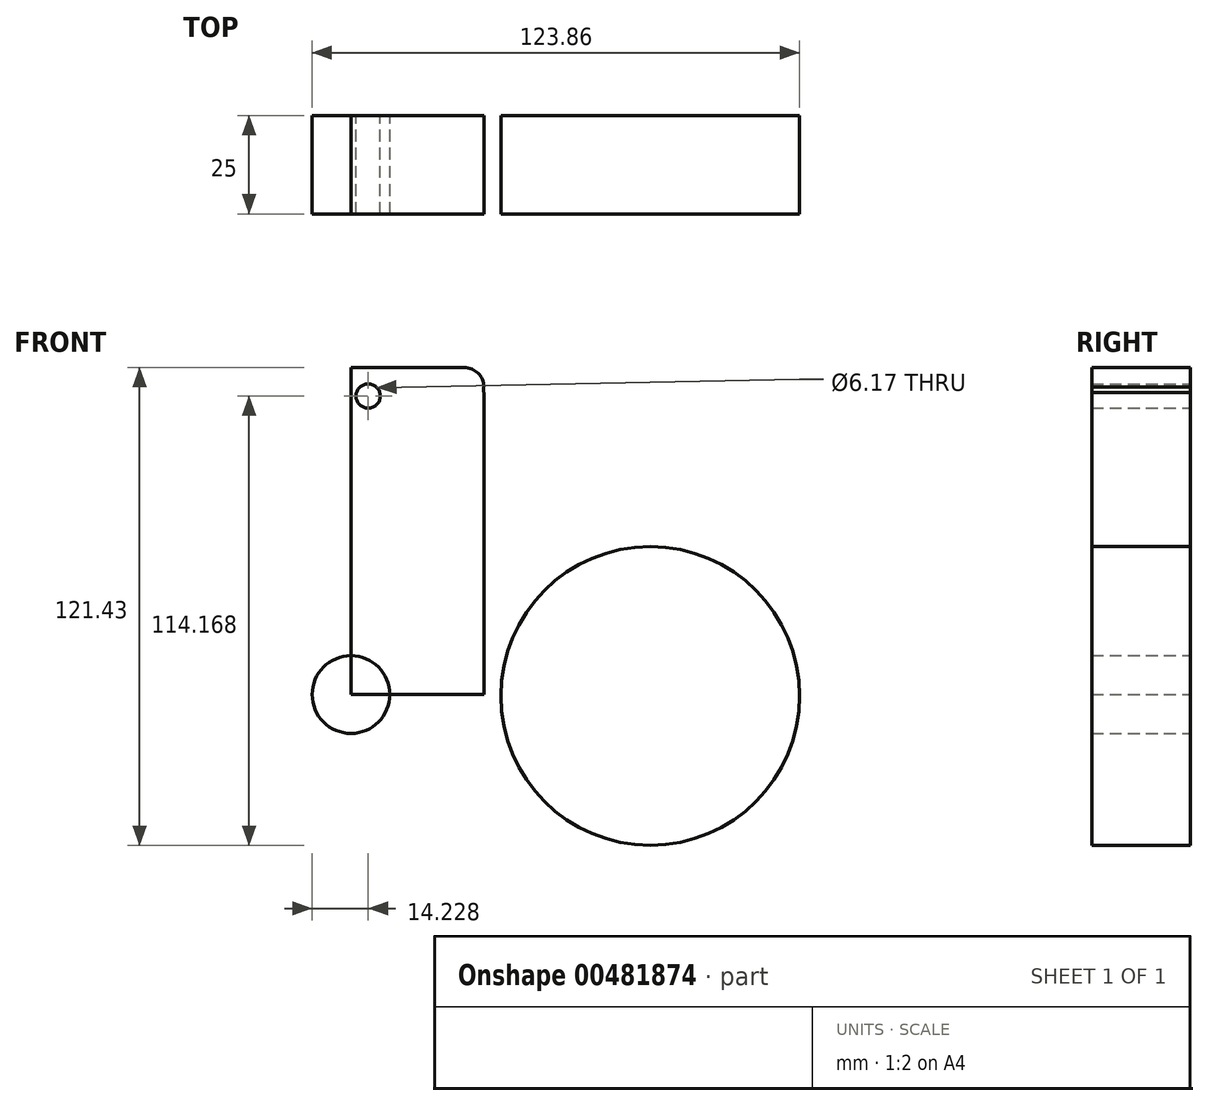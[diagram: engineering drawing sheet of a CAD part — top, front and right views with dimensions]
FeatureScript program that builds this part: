
annotation { "Feature Type Name" : "Feature", "Feature Type Description" : "" }
export const myFeature = defineFeature(function(context is Context, id is Id, definition is map)
    precondition{}
    {
        {
            var Q0;
            Q0=qCreatedBy(makeId("Front.planeOp"),FACE);
            var sketch = newSketch(context, id + "F0", { "sketchPlane" : qUnion([Q0])});
            skLineSegment(sketch, "E0.bottom", {"start": v(-17.06, -14.88) * mm, "end": v(-50.8, -14.88) * mm});
            skLineSegment(sketch, "E0.top", {"start": v(-22.06, 68.23) * mm, "end": v(-50.8, 68.23) * mm});
            skLineSegment(sketch, "E0.left", {"start": v(-17.06, -14.88) * mm, "end": v(-17.06, 63.23) * mm});
            skLineSegment(sketch, "E0.right", {"start": v(-50.8, -14.88) * mm, "end": v(-50.8, 68.23) * mm});
            skPoint(sketch, "E0.middle", {"position": v(-33.93, 26.67) * mm});
            skCircle(sketch, "E1", {"center": v(25.22, -15.24) * mm, "radius": 37.96 * mm});
            skLineSegment(sketch, "E2", {"start": v(-17.06, -14.88) * mm, "end": v(-9, -31.67) * mm});
            skCircle(sketch, "E3", {"center": v(-50.8, -14.88) * mm, "radius": 9.87 * mm});
            skPoint(sketch, "E4.visualSharp", {"position": v(-17.06, 68.23) * mm});
            skArc(sketch, "E4.filletArc", {"start": v(-17.06, 63.23) * mm, "mid": v(-18.52, 66.76) * mm, "end": v(-22.06, 68.23) * mm});
            skFitSpline(sketch, "E5", {"points": [v(-17.06, 61.88) * mm, v(-17.06, 63.23) * mm, v(15.94, 21.56) * mm], "startDerivative": vector(-2.63, 13.82) * mm, "endDerivative": vector(54.8, -73.35) * mm});
            skCircle(sketch, "E6", {"center": v(-46.45, 60.97) * mm, "radius": 3.08 * mm});
            skCircle(sketch, "E7.MirrorC", {"center": v(-46.45, 75.48) * mm, "radius": 3.08 * mm});
            skSolve(sketch);
        }
        {
            var Q0;
            {var subQ0=sQuery(id+"F0.wireOp",EDGE,"E1");var subQ1=makeQuery(id+"F0.imprint","INTERSECT",VERTEX,{"derivedFrom":[subQ0,sQuery(id+"F0.wireOp",EDGE,"E2")]});Q0=makeQuery(id+"F0.imprint","IMPRINT",FACE,{"disambiguationData":[TD([[makeQuery(id+"F0.imprint","IMPRINT",EDGE,{"disambiguationData":[TD([[subQ1,1.0]])],"derivedFrom":subQ0}),1.0]])]});}
            var Q1;
            {var subQ1=sQuery(id+"F0.wireOp",EDGE,"E0.top");Q1=makeQuery(id+"F0.imprint","IMPRINT",FACE,{"disambiguationData":[TD([[makeQuery(id+"F0.imprint","IMPRINT",EDGE,{"derivedFrom":subQ1}),1.0]])]});}
            var Q2;
            {var subQ0=sQuery(id+"F0.wireOp",EDGE,"E0.right");var subQ1=sQuery(id+"F0.wireOp",EDGE,"E0.bottom");var subQ2=makeQuery(id+"F0.imprint","INTERSECT",VERTEX,{"derivedFrom":[subQ1,subQ0]});Q2=makeQuery(id+"F0.imprint","IMPRINT",FACE,{"disambiguationData":[TD([[makeQuery(id+"F0.imprint","IMPRINT",EDGE,{"disambiguationData":[TD([[subQ2,1.0]])],"derivedFrom":subQ1}),1.0]])]});}
            extrude(context, id + "F1", {"entities" : qUnion([Q0, Q1, Q2]), "depth" : 25 * mm});
        }
    });
